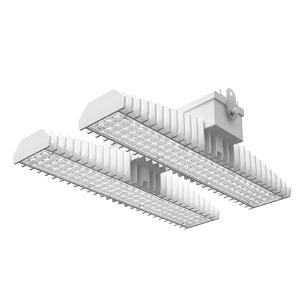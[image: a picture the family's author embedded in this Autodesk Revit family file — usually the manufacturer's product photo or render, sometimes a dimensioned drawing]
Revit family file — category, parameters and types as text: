
# Revit family: 3f_filippi_-_3f_lem_ho_medio_3f_filippi_-_58965_a0811_-_3f_lem_2_ho_led_140_cr_medio___vt_4882
name_source: partatom
category: Lighting Fixtures
units: mm (PartAtom-declared; Revit-internal decimal feet)

## family parameters
Cut with Voids When Loaded = No
Host = Face
Light Source = No
Part Type = Normal
Room Calculation Point = No
Round Connector Dimension = Use Diameter
Shared = No

## types (1)
- 3F Filippi - 3F LEM HO Medio (1 x LED, 20597 lm, 138 W, 4000 K)
    Apparent Load = 138 VA
    Approval mark = CE
    CIE Flux Codes = 83 96 99 100 100
    Color Rendering = 80
    Color Temperature = 4000 K
    Control Gear = Electronic ballast
    Default Elevation = 1800 mm
    Description = Industrial luminaire with high light output and high luminous efficiency designed with the most innovative technologies for environments with temperature up to 55°C.

ILLUMINOTECHNICAL
Luminous efficiency 100% (DLOR 99%, ULOR 1%).
Initial luminous flux of the luminaire 20597 lm.
Medium distribution with rectangular shape.
Installation Interdistance Transv.D = 1.17 x hu - Long.D = 1.21 x hu.
Tabular UGR (CIE 117 - 4H-8H; S=0.25H; 70/50/20): RUG 19.2 - 18.8.
Beam angle: 65° - 67°.
Luminous efficacy 149 lm/W.
Lifetime (L93/B10): 30000 h. (tq+25°C)
Lifetime (L90/B10): 50000 h. (tq+25°C)
Lifetime (L85/B10): 80000 h. (tq+25°C)
Lifetime (L80/B10): 100000 h. (tq+25°C)
Lifetime (L85/B10): 50000 h. (tq+55°C)
Sudden decreased luminous flux after 50000 hours: 0% (C0).
Photobiological safety in compliance with IEC/TR 62778: RG0 risk exempt, (IEC 62471).
In compliance with IEC/EN 62722-2-1 - IEC/EN 62717 standards.

SOURCE
2 Mid-Power linear LED modules 70W/840.
Energy efficiency class (UE 2019/2020 - UE 2019/2015): C.
CIE 13.3 Colour rendering index: CRI >80 (R9 <50%).
IES TM-30 Fidelity Index: Rf = 84 Rg = 95.
CCT nominal colour temperature 4000 K.
Colour initial tolerance (MacAdam): SDCM 3.

MECHANICAL
Passive modular heatsinks in die-casted aluminium, painted in white colour.
To optimize the thermal management of the LED module, the heatsinks are oversized and provided with self-cleaning of cooling fins.
Wiring body in aluminium and galvanised steel anchored solidly to the sinks and thermally separated.
3F Lens lenses with high luminous efficiency, transparent methacrylate (PMMA), fixed to the LED modules.
Fixing brackets in stainless steel.
Luminaire with limited surface temperature. - D - (EN 60598-2-24)
Dimensions: 470x542 mm, height 133 mm. Weight 10.084 kg.
IP65 protection degree.
Mechanical strength to impacts IK06 (1 joule).
Glow-wire test resistance 650°C.

ELECTRICAL
Halogen Free electronic wiring 230V-50/60Hz, power factor 0.97, THD <25%, constant output current, class I, 1 driver.
Power of the luminaire 138 W.
ENEC - CE.
SAFE FLICKER: PstLM=<1 and SVM=<0.4 (IEC TR 61547-1 and IEC TR 63158), to ensure a more comfortable and safe light.
Luminaire compliant with EN 60598-2-22 for power supply from a centralised emergency system CPSS (Central Power Supply System), not incorporated in the luminaire - high risk areas excluded. The default power and flux are 100% in AC and 100% in DC.
Ambient temperature from -30°C to +55°C.
Temperature class T6 max 85°C.
Quick connection via M20 3P connector with 9-13 mm tightening range.
Power unit positioned on a separate compartment by the LED module to ensure optimum temperatures of cabling components, to be inspectable and maintainable.
Relative humidity UR: <85%.

INSTALLATION
Ceiling / Suspended / Wall.
All accessories dedicated to this product are available on the Catalog and on our website www.3F-Filippi.com.

ACCESSORIES
A0811 - VT transparent glass, tempered, not flammable, with sealing gasket.
One required for each light module. The pack contains 10 pieces.

APPLICATIONS
In commercial environments, exhibition and industrial areas, stores, open areas.
Environments in which it is necessary a total protection against falling fragments (eg environments with foodstuffs or machines with moving parts or with extreme temperature changes), use luminaires with polycarbonate lenses.

WARNING
Fixture not suitable for cold stores with an ambient temperature <0°C and/or relative humidity >85%.
Luminaire designed for disposal/recycling at end-of-life.
Replaceable (LED only) light source by a professional. Replaceable control gear by a professional.
    Height = 133 mm  [stored 0.436352 ft]
    Lamp = 1 x LED
    Lamp Light Flux = 20597 lm
    Lamp Power = 138 W
    Lamp count = 1
    Length = 470 mm
    Lifetime = 50000 h
    Luminous efficacy = 149 lm/W
    Manufacturer = 3F Filippi
    ModVariant = No
    Model = 3F Filippi - 58965+A0811 - 3F LEM 2 HO LED 140 CR MEDIO + VT
    Mounting Place = Ceiling
    Mounting Type = Pendant
    Number of Poles = 1
    OnlyDefault = Yes
    Power Factor = 1
    Product Name = 3F Filippi - 3F LEM HO Medio
    Product group = pendant luminaire
    ProductGroupID = 9
    Protection Class = Protection class I
    Protection Degree = IP 65
    RLX_Detail_Level = 1
    RLX_Emergency_Light_Flux = 0 lm
    RLX_Emergency_Type = 0
    RLX_Emergency_Type_DB = No
    RlxData = <blob elided: 102217 chars, md5=f0dfc44a>
    Socket = socket
    Standby Power = 0 W
    System Light Flux = 20597 lm
    System Power = 138 W
    Type Comments = Product without accessories
    Type Image = 3f_filippi_-_lem_2__a0811.jpg
    URL = http://relux.com
    VarID = ---
    Voltage = 0 V
    Weight = 0.00 kg
    Width = 542 mm

note: [stored X ft] marks values corroborated as IEEE doubles in the binary element streams (Revit-internal decimal feet)

## geometry (parser evidence)
native form markers: Blend x4, Sweep x14
no freeform markers — native parametric forms only
